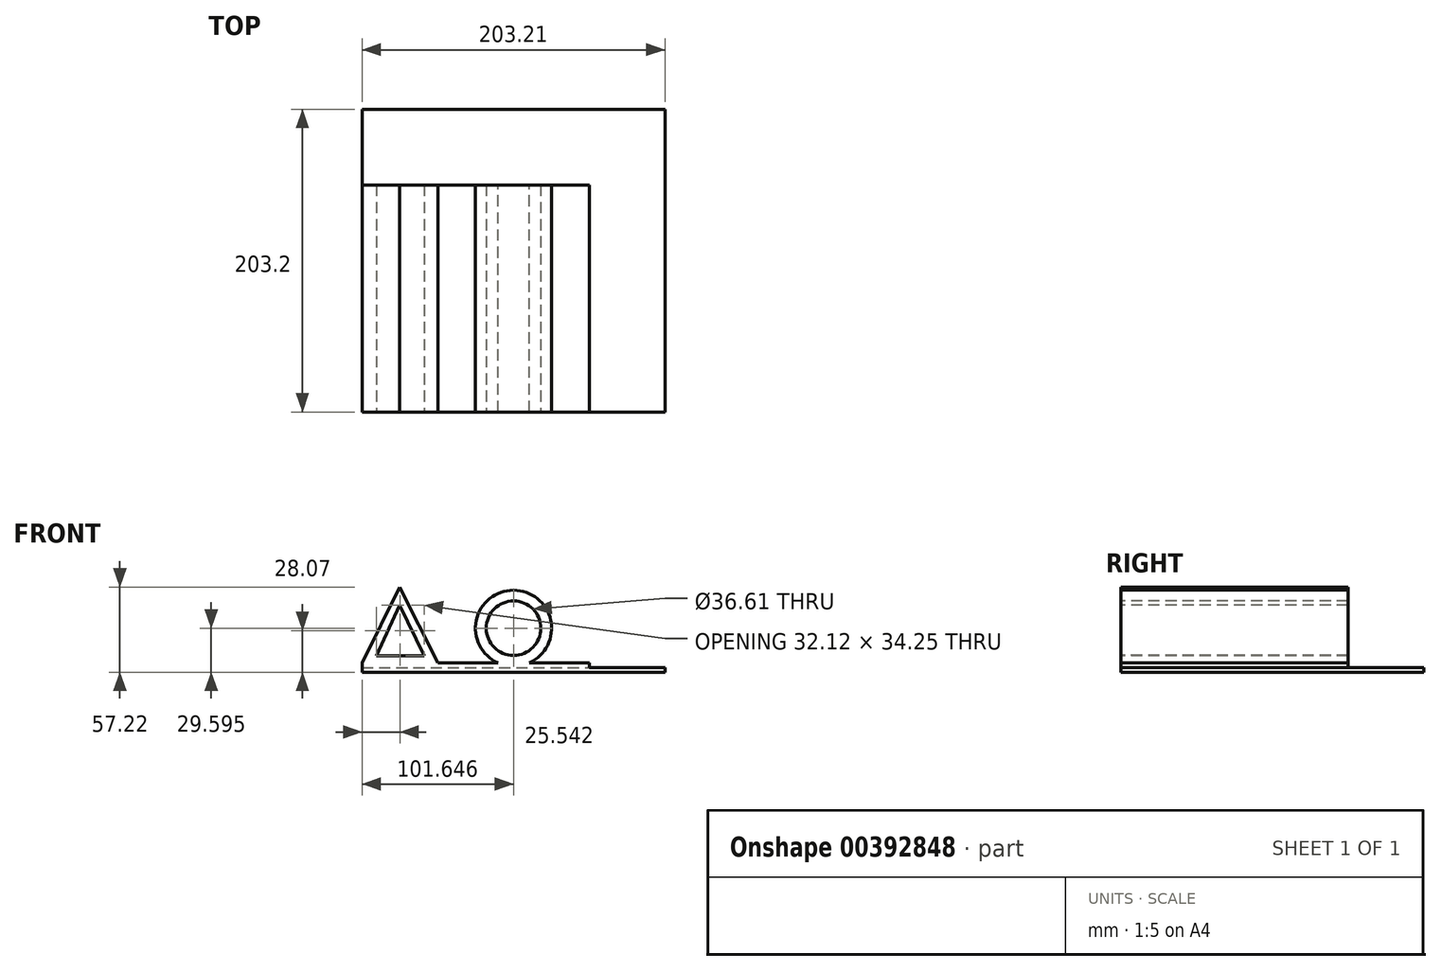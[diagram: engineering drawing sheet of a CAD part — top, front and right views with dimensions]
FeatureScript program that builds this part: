
annotation { "Feature Type Name" : "Feature", "Feature Type Description" : "" }
export const myFeature = defineFeature(function(context is Context, id is Id, definition is map)
    precondition{}
    {
        {
            var Q0;
            Q0=qCreatedBy(makeId("Top.planeOp"),FACE);
            var sketch = newSketch(context, id + "F0", { "sketchPlane" : qUnion([Q0])});
            skLineSegment(sketch, "E0.bottom", {"start": v(101.6, -101.6) * mm, "end": v(-101.6, -101.6) * mm});
            skLineSegment(sketch, "E0.top", {"start": v(101.6, 101.6) * mm, "end": v(-101.6, 101.6) * mm});
            skLineSegment(sketch, "E0.left", {"start": v(101.6, -101.6) * mm, "end": v(101.6, 101.6) * mm});
            skLineSegment(sketch, "E0.right", {"start": v(-101.6, -101.6) * mm, "end": v(-101.6, 101.6) * mm});
            skPoint(sketch, "E0.middle", {"position": v(0, 0) * mm});
            skSolve(sketch);
        }
        {
            var Q0;
            Q0=makeQuery(id+"F0.imprint","IMPRINT",FACE,{"disambiguationData":[TD([[makeQuery(id+"F0.imprint","IMPRINT",EDGE,{"derivedFrom":sQuery(id+"F0.wireOp",EDGE,"E0.bottom")}),-1.0]])]});
            extrude(context, id + "F1", {"entities" : qUnion([Q0]), "depth" : 6.35 * mm});
        }
        {
            var Q0;
            Q0=makeQuery(id+"F1.opExtrude","CAP_FACE",FACE,{"disambiguationData":[OSD([sQuery(id+"F0.wireOp",EDGE,"E0.bottom"),sQuery(id+"F0.wireOp",EDGE,"E0.top"),sQuery(id+"F0.wireOp",EDGE,"E0.left"),sQuery(id+"F0.wireOp",EDGE,"E0.right")])],"isStart":false});
            var sketch = newSketch(context, id + "F2", { "sketchPlane" : qUnion([Q0])});
            skLineSegment(sketch, "E1.bottom", {"start": v(-105.25, 101.6) * mm, "end": v(123.35, 101.6) * mm});
            skLineSegment(sketch, "E1.top", {"start": v(-105.25, 50.8) * mm, "end": v(123.35, 50.8) * mm});
            skLineSegment(sketch, "E1.left", {"start": v(-105.25, 101.6) * mm, "end": v(-105.25, 50.8) * mm});
            skLineSegment(sketch, "E1.right", {"start": v(123.35, 101.6) * mm, "end": v(123.35, 50.8) * mm});
            skSolve(sketch);
        }
        {
            var Q0;
            Q0 = qSketchRegion(id + "F2", true);
            extrude(context, id + "F3", {"entities" : qUnion([Q0]), "operationType" : NewBodyOperationType.REMOVE, "oppositeDirection" : true, "depth" : 3.17 * mm});
        }
        {
            var Q0;
            Q0=makeQuery(id+"F1.opExtrude","CAP_FACE",FACE,{"disambiguationData":[OSD([sQuery(id+"F0.wireOp",EDGE,"E0.bottom"),sQuery(id+"F0.wireOp",EDGE,"E0.top"),sQuery(id+"F0.wireOp",EDGE,"E0.left"),sQuery(id+"F0.wireOp",EDGE,"E0.right")])],"isStart":false});
            var sketch = newSketch(context, id + "F4", { "sketchPlane" : qUnion([Q0])});
            skLineSegment(sketch, "E2.bottom", {"start": v(101.6, 50.8) * mm, "end": v(50.8, 50.8) * mm});
            skLineSegment(sketch, "E2.top", {"start": v(101.6, -177.8) * mm, "end": v(50.8, -177.8) * mm});
            skLineSegment(sketch, "E2.left", {"start": v(101.6, 50.8) * mm, "end": v(101.6, -177.8) * mm});
            skLineSegment(sketch, "E2.right", {"start": v(50.8, 50.8) * mm, "end": v(50.8, -177.8) * mm});
            skSolve(sketch);
        }
        {
            var Q0;
            {var subQ0=sQuery(id+"F4.wireOp",EDGE,"E2.bottom");Q0=makeQuery(id+"F4.imprint","IMPRINT",FACE,{"disambiguationData":[TD([[makeQuery(id+"F4.imprint","IMPRINT",EDGE,{"derivedFrom":subQ0}),-1.0]])]});}
            extrude(context, id + "F5", {"entities" : qUnion([Q0]), "operationType" : NewBodyOperationType.REMOVE, "oppositeDirection" : true, "depth" : 3.17 * mm});
        }
        {
            var Q0;
            Q0=qCreatedBy(makeId("Front.planeOp"),FACE);
            var sketch = newSketch(context, id + "F6", { "sketchPlane" : qUnion([Q0])});
            skLineSegment(sketch, "E3", {"start": v(-101.61, 6.34) * mm, "end": v(-76.26, 57.22) * mm});
            skLineSegment(sketch, "E4", {"start": v(-76.26, 57.22) * mm, "end": v(-50.83, 6.31) * mm});
            skLineSegment(sketch, "E5", {"start": v(-50.83, 6.31) * mm, "end": v(-101.61, 6.34) * mm});
            skSolve(sketch);
        }
        {
            var Q0;
            Q0=makeQuery(id+"F6.imprint","IMPRINT",FACE,{"disambiguationData":[TD([[makeQuery(id+"F6.imprint","IMPRINT",EDGE,{"derivedFrom":sQuery(id+"F6.wireOp",EDGE,"E3")}),-1.0]])]});
            extrude(context, id + "F7", {"entities" : qUnion([Q0]), "operationType" : NewBodyOperationType.ADD, "depth" : 101.6 * mm});
        }
        {
            var Q0;
            Q0=makeQuery(id+"F7.opExtrude","CAP_FACE",FACE,{"disambiguationData":[OSD([sQuery(id+"F6.wireOp",EDGE,"E3"),sQuery(id+"F6.wireOp",EDGE,"E4"),sQuery(id+"F6.wireOp",EDGE,"E5")])],"isStart":true});
            extrude(context, id + "F8", {"entities" : qUnion([Q0]), "operationType" : NewBodyOperationType.ADD, "depth" : 50.8 * mm});
        }
        {
            var Q0;
            Q0=qCreatedBy(makeId("Front.planeOp"),FACE);
            var sketch = newSketch(context, id + "F9", { "sketchPlane" : qUnion([Q0])});
            skLineSegment(sketch, "E6", {"start": v(-92.13, 10.94) * mm, "end": v(-60, 10.94) * mm});
            skLineSegment(sketch, "E7", {"start": v(-60, 10.94) * mm, "end": v(-76.4, 45.2) * mm});
            skLineSegment(sketch, "E8", {"start": v(-76.4, 45.2) * mm, "end": v(-92.13, 10.94) * mm});
            skSolve(sketch);
        }
        {
            var Q0;
            Q0 = qSketchRegion(id + "F9", true);
            extrude(context, id + "F10", {"entities" : qUnion([Q0]), "operationType" : NewBodyOperationType.REMOVE, "endBound" : BoundingType.SYMMETRIC, "oppositeDirection" : true, "depth" : 203.2 * mm});
        }
        {
            var Q0;
            Q0=qCreatedBy(makeId("Front.planeOp"),FACE);
            var sketch = newSketch(context, id + "F11", { "sketchPlane" : qUnion([Q0])});
            skCircle(sketch, "E9", {"center": v(0.04, 29.6) * mm, "radius": 25.53 * mm});
            skSolve(sketch);
        }
        {
            var Q0;
            Q0=makeQuery(id+"F11.imprint","IMPRINT",FACE,{"disambiguationData":[TD([[makeQuery(id+"F11.imprint","IMPRINT",EDGE,{"derivedFrom":sQuery(id+"F11.wireOp",EDGE,"E9")}),1.0]])]});
            extrude(context, id + "F12", {"entities" : qUnion([Q0]), "operationType" : NewBodyOperationType.ADD, "depth" : 101.6 * mm});
        }
        {
            var Q0;
            Q0=makeQuery(id+"F12.opExtrude","CAP_FACE",FACE,{"disambiguationData":[OSD([sQuery(id+"F11.wireOp",EDGE,"E9")])],"isStart":true});
            extrude(context, id + "F13", {"entities" : qUnion([Q0]), "operationType" : NewBodyOperationType.ADD, "depth" : 50.8 * mm});
        }
        {
            var Q0;
            Q0=makeQuery(id+"F12.boolean.opBoolean","MERGE",FACE,{"derivedFrom":[makeQuery(id+"F7.boolean.opBoolean","MERGE",FACE,{"derivedFrom":[makeQuery(id+"F1.opExtrude","SWEPT_FACE",FACE,{"disambiguationData":[OSD([sQuery(id+"F0.wireOp",EDGE,"E0.bottom")])]}),makeQuery(id+"F7.opExtrude","CAP_FACE",FACE,{"disambiguationData":[OSD([sQuery(id+"F6.wireOp",EDGE,"E3"),sQuery(id+"F6.wireOp",EDGE,"E4"),sQuery(id+"F6.wireOp",EDGE,"E5")])],"isStart":false})]}),makeQuery(id+"F12.opExtrude","CAP_FACE",FACE,{"disambiguationData":[OSD([sQuery(id+"F11.wireOp",EDGE,"E9")])],"isStart":false})]});
            var sketch = newSketch(context, id + "F14", { "sketchPlane" : qUnion([Q0])});
            skCircle(sketch, "E10", {"center": v(0.04, 29.6) * mm, "radius": 18.3 * mm});
            skSolve(sketch);
        }
        {
            var Q0;
            Q0=makeQuery(id+"F14.imprint","IMPRINT",FACE,{"disambiguationData":[TD([[makeQuery(id+"F14.imprint","IMPRINT",EDGE,{"derivedFrom":sQuery(id+"F14.wireOp",EDGE,"E10")}),1.0]])]});
            var Q1;
            Q1=sQuery(id+"F14.wireOp",EDGE,"E10");
            extrude(context, id + "F15", {"entities" : qUnion([Q0]), "operationType" : NewBodyOperationType.REMOVE, "surfaceEntities" : qUnion([Q1]), "oppositeDirection" : true, "depth" : 203.2 * mm});
        }
    });
